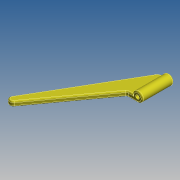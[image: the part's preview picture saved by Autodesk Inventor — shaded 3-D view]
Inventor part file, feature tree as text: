
AUTODESK INVENTOR PART (.ipt)
format: ipt  version: 2019 (Build 230136000, 136)  size: 299,520 bytes
history: native  units: mm
features: fillet x7, extrude x3, sketch x3, hole x1, plane x1, projected_geometry x1
ambient origin geometry x8: Origin, YZ Plane, XZ Plane, XY Plane, X Axis, Y Axis, Z Axis, Center Point
bodies: Solid3 (feature_tree)
feature tree (16):
  extrude  "Extrusion5"  Depth=4.0mm
  extrude  "Extrusion6"  Depth=4.0mm
  fillet  "Fillet10"  Radius=0.1mm
  fillet  "Fillet15"  Radius=4.0mm
  fillet  "Fillet16"  Radius=4.0mm
  fillet  "Fillet17"  Radius=4.0mm
  hole  "Hole4"  [1 undecoded]
  fillet  "Fillet18"  Radius=4.0mm
  extrude  "Extrusion7"  Depth=2.0mm
  fillet  "Fillet19"  Radius=1.0mm
  fillet  "Fillet20"  Radius=1.0mm
  plane  "Work Plane1"
  sketch  "Sketch5"  dims[d0=4.0mm d6=20.0mm d7=46.0mm d8=8.0mm d9=8.5mm d30=6.0mm]
  sketch  "Sketch7"  dims[d31=32.0mm d32=50.0mm d48=0.1mm d49=4.0mm d50=0.0mm d52=4.0mm d53=0.0mm d54=4.0mm]
  sketch  "Sketch8"  dims[d66=8.0mm d67=4.0mm d68=4.0mm d69=2.0mm d70=3.0mm d71=6.0mm d72=4.0mm d73=2.0mm d74=90.0deg d75=8.0mm d76=20.594885mm d77=1.0mm d78=1.0mm d79=4.0mm d81=0.2mm d82=0.0mm d83=0.2mm d84=0.2mm d86=1.5mm d87=-5.0mm]
  projected_geometry  "Project Cut Edges3"
note: 1 required parameter value undecoded (feature->parameter linkage not recoverable at this tier; creation-order binding heuristic only, values carry confidence <= 0.55)
